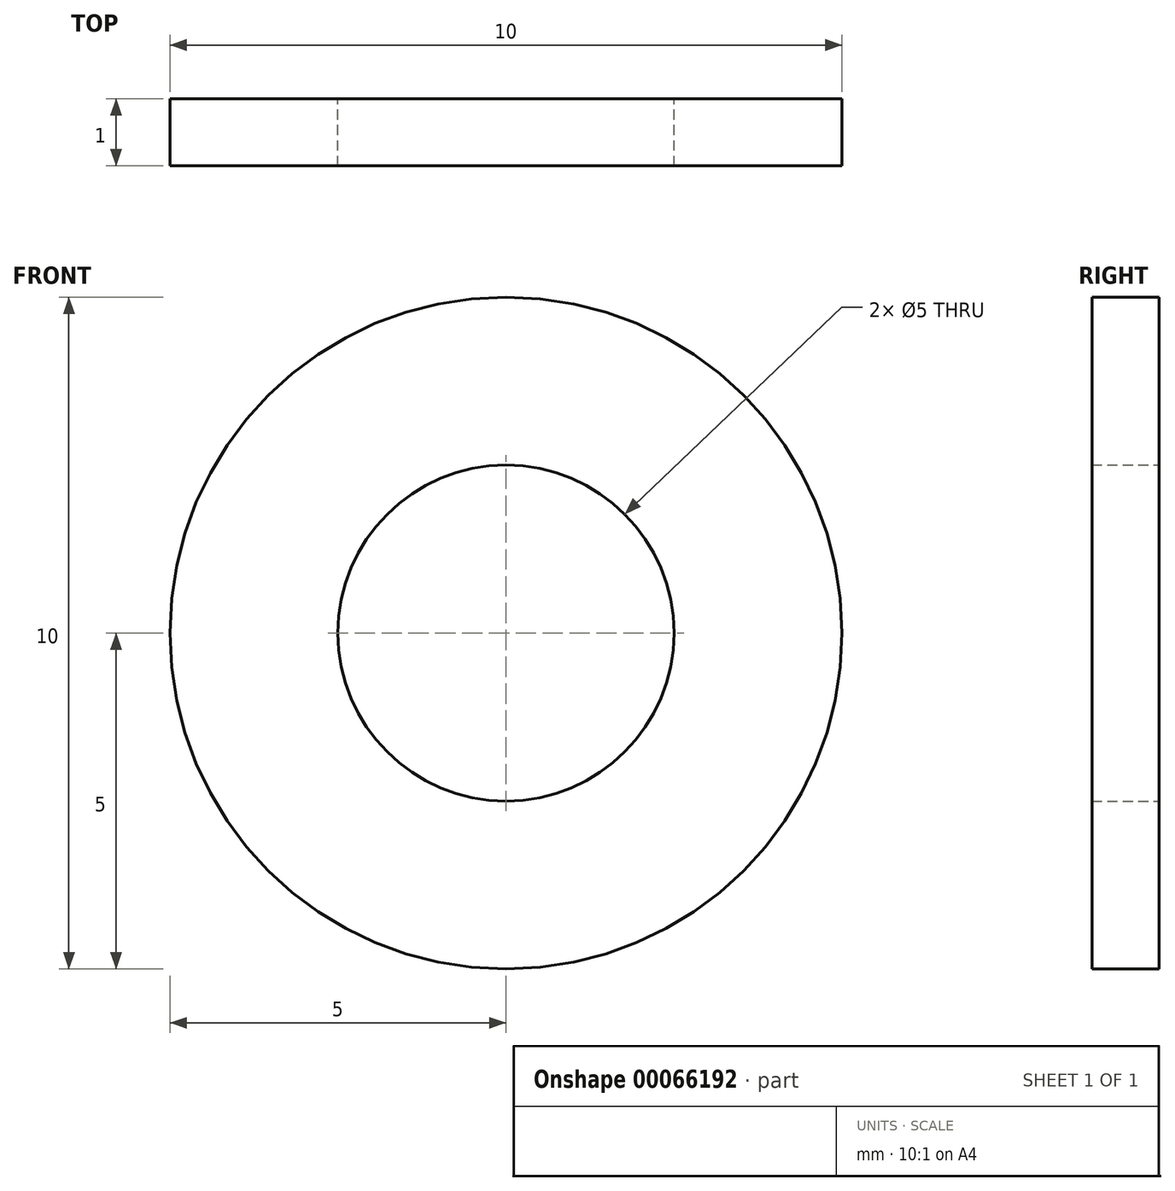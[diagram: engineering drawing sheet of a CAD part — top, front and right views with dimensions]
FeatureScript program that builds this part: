
annotation { "Feature Type Name" : "Feature", "Feature Type Description" : "" }
export const myFeature = defineFeature(function(context is Context, id is Id, definition is map)
    precondition{}
    {
        {
            var Q0;
            Q0=qCreatedBy(makeId("Front.planeOp"),FACE);
            var sketch = newSketch(context, id + "F0", { "sketchPlane" : qUnion([Q0])});
            skCircle(sketch, "E0", {"center": v(0, 0) * mm, "radius": 2.5 * mm});
            skCircle(sketch, "E1", {"center": v(0, 0) * mm, "radius": 5 * mm});
            skSolve(sketch);
        }
        {
            var Q0;
            Q0=makeQuery(id+"F0.imprint","IMPRINT",FACE,{"disambiguationData":[TD([[makeQuery(id+"F0.imprint","IMPRINT",EDGE,{"derivedFrom":sQuery(id+"F0.wireOp",EDGE,"E0")}),-1.0]])]});
            extrude(context, id + "F1", {"entities" : qUnion([Q0]), "depth" : 1 * mm, "symmetric" : true});
        }
    });
